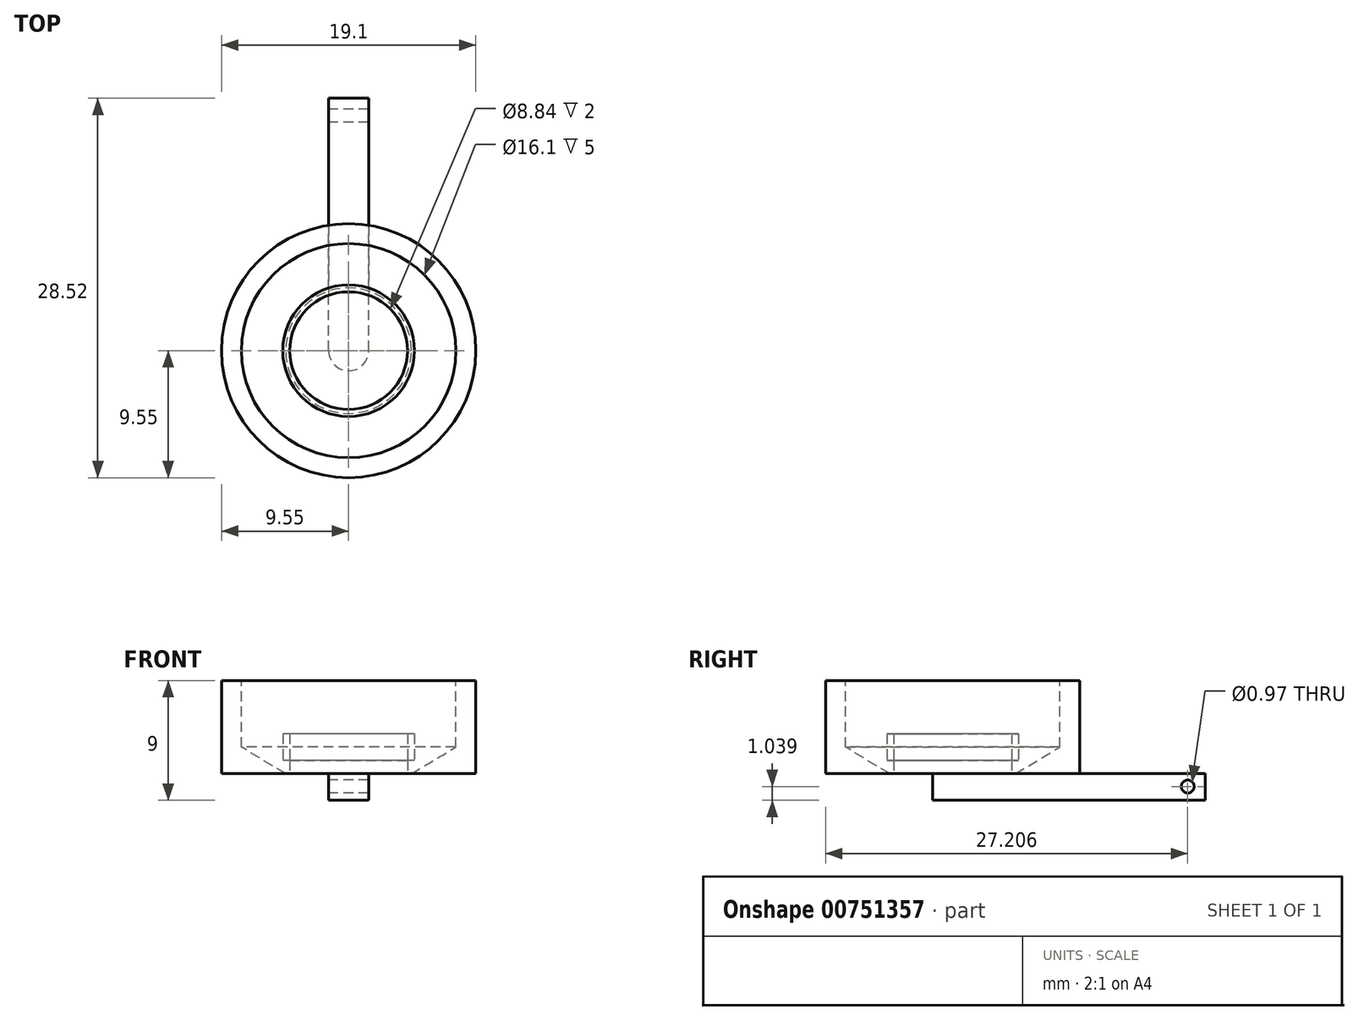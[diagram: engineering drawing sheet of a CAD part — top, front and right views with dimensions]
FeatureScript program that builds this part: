
annotation { "Feature Type Name" : "Feature", "Feature Type Description" : "" }
export const myFeature = defineFeature(function(context is Context, id is Id, definition is map)
    precondition{}
    {
        {
            var Q0;
            Q0=qCreatedBy(makeId("Top.planeOp"),FACE);
            var sketch = newSketch(context, id + "F0", { "sketchPlane" : qUnion([Q0])});
            skCircle(sketch, "E0", {"center": v(0, 0) * mm, "radius": 9.55 * mm});
            skSolve(sketch);
        }
        {
            var Q0;
            Q0=makeQuery(id+"F0.imprint","IMPRINT",FACE,{"disambiguationData":[TD([[makeQuery(id+"F0.imprint","IMPRINT",EDGE,{"derivedFrom":sQuery(id+"F0.wireOp",EDGE,"E0")}),1.0]])]});
            extrude(context, id + "F1", {"entities" : qUnion([Q0]), "depth" : 7 * mm, "offsetDistance" : 25 * mm});
        }
        {
            var Q0;
            Q0=makeQuery(id+"F1.opExtrude","CAP_FACE",FACE,{"disambiguationData":[OSD([sQuery(id+"F0.wireOp",EDGE,"E0")])],"isStart":false});
            var sketch = newSketch(context, id + "F2", { "sketchPlane" : qUnion([Q0])});
            skCircle(sketch, "E1", {"center": v(0, 0) * mm, "radius": 8.05 * mm});
            skSolve(sketch);
        }
        {
            var Q0;
            Q0=sQuery(id+"F2.wireOp",VERTEX,"E1.center");
            var Q1;
            Q1=makeQuery(id+"F1.opExtrude","SWEPT_BODY",BODY,{"disambiguationData":[OSD([sQuery(id+"F0.wireOp",EDGE,"E0")])]});
            hole(context, id + "F3", {"style" : HoleStyle.SIMPLE, "endStyle" : HoleEndStyle.BLIND, "holeDiameter" : 16.1 * mm, "majorDiameter" : 5 * mm, "holeDepth" : 5 * mm, "isTappedThrough" : true, "tappedDepth" : 12 * mm, "tapClearance" : 3, "locations" : qUnion([Q0]), "scope" : qUnion([Q1])});
        }
        {
            var Q0;
            Q0=qCreatedBy(makeId("Top.planeOp"),FACE);
            var sketch = newSketch(context, id + "F4", { "sketchPlane" : qUnion([Q0])});
            skCircle(sketch, "E2", {"center": v(0, 0) * mm, "radius": 4.42 * mm});
            skSolve(sketch);
        }
        {
            var Q0;
            Q0=makeQuery(id+"F4.imprint","IMPRINT",FACE,{"disambiguationData":[TD([[makeQuery(id+"F4.imprint","IMPRINT",EDGE,{"derivedFrom":sQuery(id+"F4.wireOp",EDGE,"E2")}),1.0]])]});
            extrude(context, id + "F5", {"entities" : qUnion([Q0]), "depth" : 1 * mm, "offsetDistance" : 25 * mm});
        }
        {
            var Q0;
            Q0=makeQuery(id+"F5.opExtrude","CAP_FACE",FACE,{"disambiguationData":[OSD([sQuery(id+"F4.wireOp",EDGE,"E2")])],"isStart":false});
            var sketch = newSketch(context, id + "F6", { "sketchPlane" : qUnion([Q0])});
            skCircle(sketch, "E3", {"center": v(0, 0) * mm, "radius": 4.95 * mm});
            skSolve(sketch);
        }
        {
            var Q0;
            Q0=makeQuery(id+"F6.imprint","IMPRINT",FACE,{"disambiguationData":[TD([[makeQuery(id+"F6.imprint","IMPRINT",EDGE,{"derivedFrom":sQuery(id+"F6.wireOp",EDGE,"E3")}),1.0]])]});
            extrude(context, id + "F7", {"entities" : qUnion([Q0]), "depth" : 2 * mm, "offsetDistance" : 25 * mm});
        }
        {
            var Q0;
            Q0=makeQuery(id+"F5.opExtrude","CAP_FACE",FACE,{"disambiguationData":[OSD([sQuery(id+"F4.wireOp",EDGE,"E2")])],"isStart":true});
            var sketch = newSketch(context, id + "F8", { "sketchPlane" : qUnion([Q0])});
            skCircle(sketch, "E4", {"center": v(0, 0) * mm, "radius": 1.5 * mm});
            skPoint(sketch, "E5.start.orphan", {"position": v(-1.5, 0) * mm});
            skPoint(sketch, "E6.start.orphan", {"position": v(1.5, 0) * mm});
            skLineSegment(sketch, "E7", {"start": v(-1.5, 0) * mm, "end": v(-1.5, -3.97) * mm});
            skLineSegment(sketch, "E8", {"start": v(-1.5, -3.97) * mm, "end": v(1.5, -3.97) * mm});
            skLineSegment(sketch, "E9", {"start": v(1.5, 0) * mm, "end": v(1.5, -3.97) * mm});
            skSolve(sketch);
        }
        {
            var Q0;
            Q0=makeQuery(id+"F8.imprint","IMPRINT",FACE,{"disambiguationData":[TD([[makeQuery(id+"F8.imprint","IMPRINT",EDGE,{"derivedFrom":sQuery(id+"F8.wireOp",EDGE,"E4")}),1.0]])]});
            var Q1;
            {var subQ0=sQuery(id+"F8.wireOp",EDGE,"E7");Q1=makeQuery(id+"F8.imprint","IMPRINT",FACE,{"disambiguationData":[TD([[makeQuery(id+"F8.imprint","IMPRINT",EDGE,{"derivedFrom":subQ0}),1.0]])]});}
            extrude(context, id + "F9", {"entities" : qUnion([Q0, Q1]), "operationType" : NewBodyOperationType.ADD, "depth" : 2 * mm, "offsetDistance" : 25 * mm});
        }
        {
            var Q0;
            Q0=makeQuery(id+"F9.opExtrude","SWEPT_FACE",FACE,{"disambiguationData":[OSD([sQuery(id+"F8.wireOp",EDGE,"E8")])]});
            var sketch = newSketch(context, id + "F10", { "sketchPlane" : qUnion([Q0])});
            skSolve(sketch);
        }
        {
            var Q0;
            {var subQ0=sQuery(id+"F8.wireOp",EDGE,"E8");Q0=makeQuery(id+"F10.imprint","IMPRINT",FACE,{"disambiguationData":[TD([[makeQuery(id+"F10.imprint","IMPRINT",EDGE,{"derivedFrom":makeQuery(id+"F9.opExtrude","CAP_EDGE",EDGE,{"disambiguationData":[OSD([subQ0])],"isStart":false})}),-1.0]])]});}
            extrude(context, id + "F11", {"entities" : qUnion([Q0]), "depth" : 15 * mm, "offsetDistance" : 25 * mm});
        }
        {
            var Q0;
            Q0=makeQuery(id+"F5.opExtrude","SWEPT_BODY",BODY,{"disambiguationData":[OSD([sQuery(id+"F4.wireOp",EDGE,"E2")])]});
            var Q1;
            Q1=makeQuery(id+"F11.opExtrude","SWEPT_BODY",BODY,{"disambiguationData":[OSD([sQuery(id+"F8.wireOp",EDGE,"E7"),sQuery(id+"F8.wireOp",EDGE,"E8"),sQuery(id+"F8.wireOp",EDGE,"E9")])]});
            var Q2;
            Q2=makeQuery(id+"F7.opExtrude","SWEPT_BODY",BODY,{"disambiguationData":[OSD([sQuery(id+"F4.wireOp",EDGE,"E2"),sQuery(id+"F6.wireOp",EDGE,"E3")])]});
            booleanBodies(context, id + "F12", {"operationType" : BooleanOperationType.UNION, "tools" : qUnion([Q0, Q1, Q2])});
        }
        {
            var Q0;
            {var subQ0=sQuery(id+"F8.wireOp",EDGE,"E7");Q0=makeQuery(id+"F12.opBoolean","MERGE",FACE,{"derivedFrom":[makeQuery(id+"F9.opExtrude","SWEPT_FACE",FACE,{"disambiguationData":[OSD([subQ0])]}),makeQuery(id+"F11.opExtrude","SWEPT_FACE",FACE,{"disambiguationData":[OSD([subQ0,sQuery(id+"F8.wireOp",EDGE,"E8")])]})]});}
            var sketch = newSketch(context, id + "F13", { "sketchPlane" : qUnion([Q0])});
            skCircle(sketch, "E10", {"center": v(-17.66, -0.96) * mm, "radius": 0.48 * mm});
            skSolve(sketch);
        }
        {
            var Q0;
            Q0=makeQuery(id+"F13.imprint","IMPRINT",FACE,{"disambiguationData":[TD([[makeQuery(id+"F13.imprint","IMPRINT",EDGE,{"derivedFrom":sQuery(id+"F13.wireOp",EDGE,"E10")}),1.0]])]});
            extrude(context, id + "F14", {"entities" : qUnion([Q0]), "operationType" : NewBodyOperationType.REMOVE, "oppositeDirection" : true, "depth" : 25 * mm, "offsetDistance" : 25 * mm});
        }
    });
